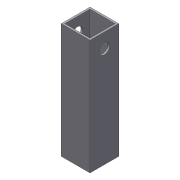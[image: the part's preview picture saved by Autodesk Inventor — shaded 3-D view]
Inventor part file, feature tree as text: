
AUTODESK INVENTOR PART (.ipt)
format: ipt  version: 2012 (Build 160160000, 160)  size: 82,944 bytes
history: native  units: in
note: dims shown in document units (in); Inventor stores cm internally (conversion verified against a paired STEP export)
features: extrude x2, sketch x2, shell x1
ambient origin geometry x8: Origin, YZ Plane, XZ Plane, XY Plane, X Axis, Y Axis, Z Axis, Center Point
bodies: Solid1 (feature_tree)
feature tree (5):
  extrude  "Extrusion1"  Depth=4.0in
  shell  "Shell1"  Thickness=1.0in
  extrude  "Extrusion2"  Depth=0.375in
  sketch  "Sketch1"  dims[d0=1.0in d1=4.0in d2=1.0in d3=0.0in]
  sketch  "Sketch2"  dims[d4=0.0625in d5=0.375in d6=0.5in d7=0.5in d8=1.0in d9=0.0in]
